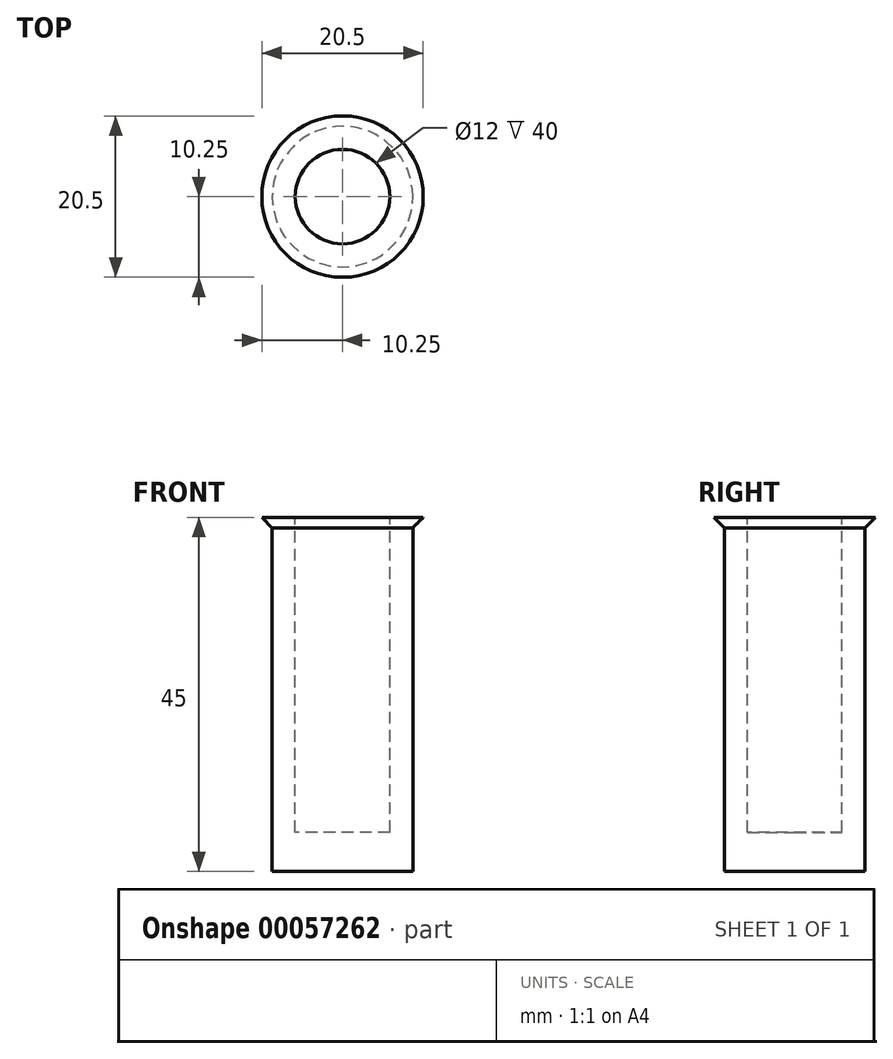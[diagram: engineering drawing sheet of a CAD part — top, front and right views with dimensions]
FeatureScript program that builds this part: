
annotation { "Feature Type Name" : "Feature", "Feature Type Description" : "" }
export const myFeature = defineFeature(function(context is Context, id is Id, definition is map)
    precondition{}
    {
        {
            var Q0;
            Q0=qCreatedBy(makeId("Top.planeOp"),FACE);
            var sketch = newSketch(context, id + "F0", { "sketchPlane" : qUnion([Q0])});
            skCircle(sketch, "E0", {"center": v(0, 0) * mm, "radius": 8.93 * mm});
            skSolve(sketch);
        }
        {
            var Q0;
            Q0=makeQuery(id+"F0.imprint","IMPRINT",FACE,{"disambiguationData":[TD([[makeQuery(id+"F0.imprint","IMPRINT",EDGE,{"derivedFrom":sQuery(id+"F0.wireOp",EDGE,"E0")}),1.0]])]});
            extrude(context, id + "F1", {"entities" : qUnion([Q0]), "depth" : 45 * mm});
        }
        {
            var Q0;
            Q0=makeQuery(id+"F1.opExtrude","CAP_FACE",FACE,{"disambiguationData":[OSD([sQuery(id+"F0.wireOp",EDGE,"E0")])],"isStart":false});
            var sketch = newSketch(context, id + "F2", { "sketchPlane" : qUnion([Q0])});
            skCircle(sketch, "E1", {"center": v(0, 0) * mm, "radius": 6 * mm});
            skSolve(sketch);
        }
        {
            var Q0;
            Q0=makeQuery(id+"F2.imprint","IMPRINT",FACE,{"disambiguationData":[TD([[makeQuery(id+"F2.imprint","IMPRINT",EDGE,{"derivedFrom":sQuery(id+"F2.wireOp",EDGE,"E1")}),1.0]])]});
            extrude(context, id + "F3", {"entities" : qUnion([Q0]), "operationType" : NewBodyOperationType.REMOVE, "oppositeDirection" : true, "depth" : 40 * mm});
        }
        {
            var Q0;
            Q0=makeQuery(id+"F1.opExtrude","CAP_FACE",FACE,{"disambiguationData":[OSD([sQuery(id+"F0.wireOp",EDGE,"E0")])],"isStart":false});
            var sketch = newSketch(context, id + "F4", { "sketchPlane" : qUnion([Q0])});
            skCircle(sketch, "E2", {"center": v(0, 0) * mm, "radius": 10.25 * mm});
            skSolve(sketch);
        }
        {
            var Q0;
            Q0=makeQuery(id+"F4.imprint","IMPRINT",FACE,{"disambiguationData":[TD([[makeQuery(id+"F4.imprint","IMPRINT",EDGE,{"derivedFrom":sQuery(id+"F4.wireOp",EDGE,"E2")}),1.0]])]});
            extrude(context, id + "F5", {"entities" : qUnion([Q0]), "operationType" : NewBodyOperationType.ADD, "oppositeDirection" : true, "depth" : 1.5 * mm});
        }
        {
            var Q0;
            Q0=makeQuery(id+"F5.opExtrude","CAP_EDGE",EDGE,{"disambiguationData":[OSD([sQuery(id+"F4.wireOp",EDGE,"E2")])],"isStart":false});
            chamfer(context, id + "F6", {"entities" : qUnion([Q0]), "width" : 1.5 * mm, "tangentPropagation" : true});
        }
    });
